# Revit family: ledporch-e_re120-5w-4000k-em1_549004004310
name_source: partatom
category: Leuchten
revit_build: Autodesk Revit 2016 (Build: 20190508_0715(x64)
units: mm (PartAtom-declared; Revit-internal decimal feet)

## family parameters
Basisbauteil = Fläche
Beim Laden mit Abzugskörper schneiden = Nein
Bemaßung runder Anschluss = Durchmesser verwenden
Gemeinsam genutzt = Nein
Lichtquelle = Nein
Raumberechnungspunkt = Nein
Teiletyp = Normal

## types (1)
- LEDPorch-E Re120-5W-4000K-EM1 (1 x LED, 500 lm)
    Approval mark = CE
    Beschreibung = Easy solution for replacing and renovating existing solutions. IP65 and high IK10 impact resistance for outdoor application. Detection range, hold time and daylight sensor settings can be easily customized via DIP switch. Energy saving up to 50% compared to compact fluorescent based fixtures. Further energy saving by the automatic dimming feature. Also suitable for outdoor applications.
    CIE Flux Codes = 44 73 91 90 100
    Control Gear = Electronic ballast
    Height = 89 mm
    Hersteller = OPPLE
    Lamp Light Flux = 500 lm
    Lamp count = 1
    Lampe = 1 x LED
    Length = 121 mm
    Luminous efficacy = 100 lm/W
    ModVariant = Nein
    Modell = 549004004310
    Mounting Place = Ceiling, Wall
    Mounting Type = Surface mounted
    Number of Poles = 1
    OnlyDefault = Ja
    Power Factor = 1
    Product Name = LEDPorch-E Re120-5W-4000K-EM1
    Product group = Porchlight EcoMax
    ProductGroupID = 320
    Protection Class = Protection class II
    Protection Degree = IP 65
    RLX_Detail_Level = 1
    RlxData = <blob elided: 132953 chars, md5=920039e7>
    Scheinlast = 5 VA
    Socket = socket
    Standby Power = 0 W
    System Light Flux = 500 lm
    System Power = 5 W
    Typenbild = 549004004310.jpg
    Typenkommentare = Product without accessories
    URL = http://relux.com
    VarID = ---
    Voltage = 0 V
    Vorgabe-Ansicht = 1800 mm
    Weight = 0.00 kg
    Width = 344 mm

## geometry (parser evidence)
native form markers: Blend x4, Sweep x15
no freeform markers — native parametric forms only
